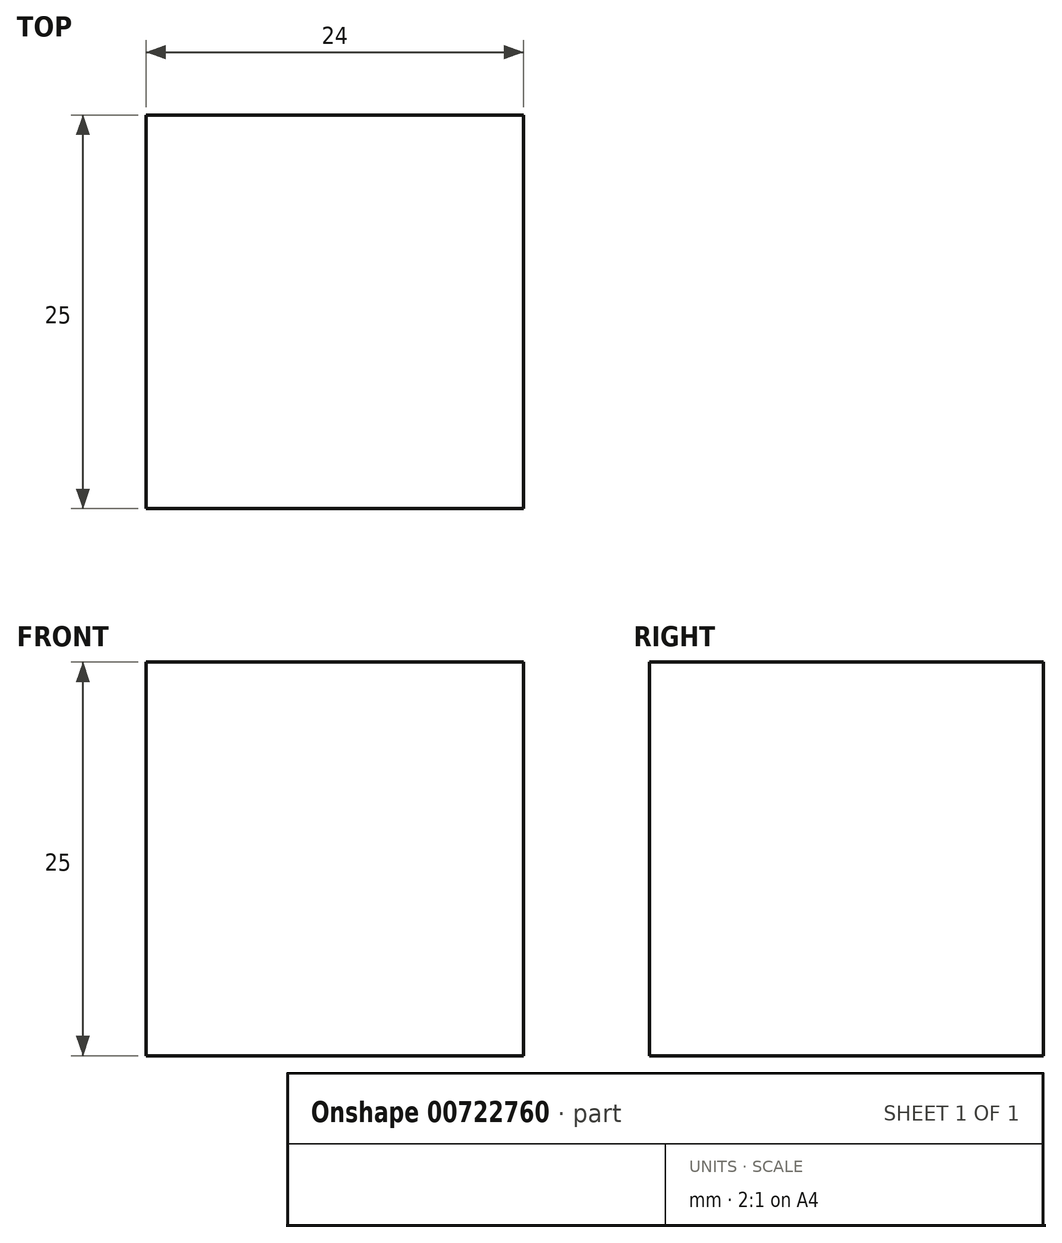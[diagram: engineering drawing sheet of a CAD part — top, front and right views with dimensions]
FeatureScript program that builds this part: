
annotation { "Feature Type Name" : "Feature", "Feature Type Description" : "" }
export const myFeature = defineFeature(function(context is Context, id is Id, definition is map)
    precondition{}
    {
        {
            var Q0;
            Q0=qCreatedBy(makeId("Front.planeOp"),FACE);
            var sketch = newSketch(context, id + "F0", { "sketchPlane" : qUnion([Q0])});
            skLineSegment(sketch, "E0.bottom", {"start": v(11.71, 12.54) * mm, "end": v(-13.29, 12.54) * mm});
            skLineSegment(sketch, "E0.top", {"start": v(11.71, -12.46) * mm, "end": v(-13.29, -12.46) * mm});
            skLineSegment(sketch, "E0.left", {"start": v(11.71, 12.54) * mm, "end": v(11.71, -12.46) * mm});
            skLineSegment(sketch, "E0.right", {"start": v(-12.29, 12.54) * mm, "end": v(-12.29, -12.46) * mm});
            skSolve(sketch);
        }
        {
            var Q0;
            Q0 = qSketchRegion(id + "F0", true);
            extrude(context, id + "F1", {"entities" : qUnion([Q0]), "endBound" : BoundingType.SYMMETRIC, "depth" : 25 * mm, "offsetDistance" : 25 * mm});
        }
    });
